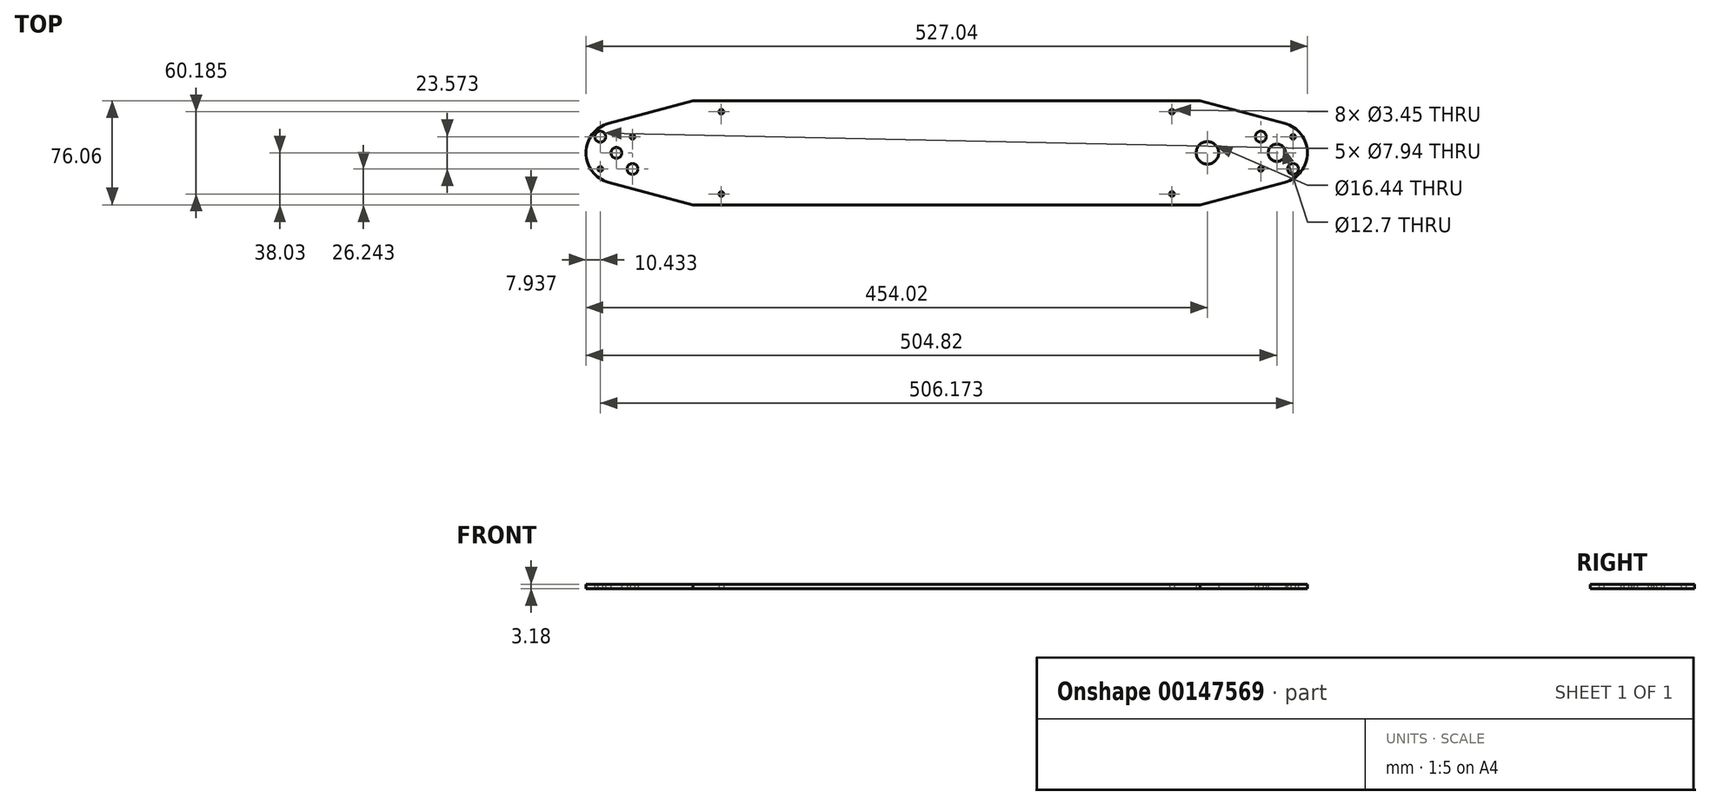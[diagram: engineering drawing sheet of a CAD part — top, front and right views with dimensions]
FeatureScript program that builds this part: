
annotation { "Feature Type Name" : "Feature", "Feature Type Description" : "" }
export const myFeature = defineFeature(function(context is Context, id is Id, definition is map)
    precondition{}
    {
        {
            var Q0;
            Q0=qCreatedBy(makeId("Top.planeOp"),FACE);
            var sketch = newSketch(context, id + "F0", { "sketchPlane" : qUnion([Q0])});
            skPoint(sketch, "E0.rect.middle", {"position": v(0, 0) * mm});
            skCircle(sketch, "E1", {"center": v(0, 0) * mm, "radius": 11.11 * mm, "construction": true});
            skLineSegment(sketch, "E2.bottom", {"start": v(11.79, 11.79) * mm, "end": v(-11.79, 11.79) * mm, "construction": true});
            skLineSegment(sketch, "E2.left", {"start": v(11.79, 11.79) * mm, "end": v(11.79, -11.79) * mm, "construction": true});
            skLineSegment(sketch, "E2.right", {"start": v(-11.79, 11.79) * mm, "end": v(-11.79, -11.79) * mm, "construction": true});
            skCircle(sketch, "E3", {"center": v(11.79, 11.79) * mm, "radius": 5.56 * mm, "construction": true});
            skCircle(sketch, "E4", {"center": v(-11.79, 11.79) * mm, "radius": 3.97 * mm});
            skCircle(sketch, "E5", {"center": v(11.79, 11.79) * mm, "radius": 1.73 * mm});
            skCircle(sketch, "E6", {"center": v(11.79, -11.79) * mm, "radius": 3.97 * mm});
            skCircle(sketch, "E7", {"center": v(-11.79, -11.79) * mm, "radius": 1.73 * mm});
            skArc(sketch, "E8", {"start": v(-488.35, 21.47) * mm, "mid": v(-504.83, 0) * mm, "end": v(-488.35, -21.47) * mm});
            skLineSegment(sketch, "E9.bottom", {"start": v(-494.39, 11.79) * mm, "end": v(-470.81, 11.79) * mm, "construction": true});
            skLineSegment(sketch, "E9.top", {"start": v(-494.39, -11.79) * mm, "end": v(-470.81, -11.79) * mm, "construction": true});
            skLineSegment(sketch, "E9.left", {"start": v(-494.39, 11.79) * mm, "end": v(-494.39, -11.79) * mm, "construction": true});
            skLineSegment(sketch, "E9.right", {"start": v(-470.81, 11.79) * mm, "end": v(-470.81, -11.79) * mm, "construction": true});
            skCircle(sketch, "E10", {"center": v(-470.81, 11.79) * mm, "radius": 1.73 * mm});
            skCircle(sketch, "E11", {"center": v(-482.6, 0) * mm, "radius": 3.97 * mm});
            skCircle(sketch, "E12", {"center": v(-494.39, 11.79) * mm, "radius": 3.97 * mm});
            skCircle(sketch, "E13", {"center": v(-494.39, -11.79) * mm, "radius": 1.73 * mm});
            skCircle(sketch, "E14", {"center": v(-470.81, -11.79) * mm, "radius": 3.97 * mm});
            skLineSegment(sketch, "E15", {"start": v(0, 0) * mm, "end": v(-482.6, 0) * mm, "construction": true});
            skLineSegment(sketch, "E16", {"start": v(-488.35, -21.47) * mm, "end": v(-426.54, -38.03) * mm});
            skLineSegment(sketch, "E17", {"start": v(-488.35, 21.47) * mm, "end": v(-426.54, 38.03) * mm});
            skLineSegment(sketch, "E18", {"start": v(-420.2, -34.86) * mm, "end": v(-62.4, -34.86) * mm, "construction": true});
            skLineSegment(sketch, "E19", {"start": v(-420.2, 34.86) * mm, "end": v(-62.4, 34.86) * mm, "construction": true});
            skLineSegment(sketch, "E20", {"start": v(-420.2, 38.03) * mm, "end": v(-420.2, 34.86) * mm, "construction": true});
            skLineSegment(sketch, "E21", {"start": v(-420.2, 38.03) * mm, "end": v(-426.54, 38.03) * mm});
            skLineSegment(sketch, "E22", {"start": v(-420.2, -34.86) * mm, "end": v(-420.2, -38.03) * mm, "construction": true});
            skLineSegment(sketch, "E23", {"start": v(-420.2, -38.03) * mm, "end": v(-426.54, -38.03) * mm});
            skLineSegment(sketch, "E24", {"start": v(-62.4, -34.86) * mm, "end": v(-62.4, -38.03) * mm, "construction": true});
            skLineSegment(sketch, "E25", {"start": v(-62.4, -38.03) * mm, "end": v(-56.06, -38.03) * mm});
            skLineSegment(sketch, "E26", {"start": v(-62.4, 34.86) * mm, "end": v(-62.4, 38.03) * mm, "construction": true});
            skLineSegment(sketch, "E27", {"start": v(-62.4, 38.03) * mm, "end": v(-56.06, 38.03) * mm});
            skLineSegment(sketch, "E28", {"start": v(-56.06, -38.03) * mm, "end": v(5.75, -21.47) * mm});
            skLineSegment(sketch, "E29", {"start": v(5.75, 21.47) * mm, "end": v(-56.06, 38.03) * mm});
            skArc(sketch, "E30", {"start": v(5.75, -21.47) * mm, "mid": v(22.23, 0) * mm, "end": v(5.75, 21.47) * mm});
            skLineSegment(sketch, "E31", {"start": v(-420.2, 34.86) * mm, "end": v(-420.2, 30.1) * mm, "construction": true});
            skLineSegment(sketch, "E32", {"start": v(-420.2, 30.1) * mm, "end": v(-405.9, 30.1) * mm, "construction": true});
            skLineSegment(sketch, "E33", {"start": v(-420.2, -34.86) * mm, "end": v(-420.2, -30.1) * mm, "construction": true});
            skLineSegment(sketch, "E34", {"start": v(-420.2, -30.1) * mm, "end": v(-405.9, -30.1) * mm, "construction": true});
            skLineSegment(sketch, "E35", {"start": v(-62.4, -34.86) * mm, "end": v(-62.4, -30.1) * mm, "construction": true});
            skLineSegment(sketch, "E36", {"start": v(-62.4, -30.1) * mm, "end": v(-76.7, -30.1) * mm, "construction": true});
            skLineSegment(sketch, "E37", {"start": v(-62.4, 34.86) * mm, "end": v(-62.4, 30.1) * mm, "construction": true});
            skLineSegment(sketch, "E38", {"start": v(-62.4, 30.1) * mm, "end": v(-76.7, 30.1) * mm, "construction": true});
            skCircle(sketch, "E39", {"center": v(-405.9, 30.1) * mm, "radius": 1.73 * mm});
            skCircle(sketch, "E40", {"center": v(-76.7, 30.1) * mm, "radius": 1.73 * mm});
            skCircle(sketch, "E41", {"center": v(-76.7, -30.1) * mm, "radius": 1.73 * mm});
            skCircle(sketch, "E42", {"center": v(-405.9, -30.1) * mm, "radius": 1.73 * mm});
            skLineSegment(sketch, "E43", {"start": v(-11.79, -11.79) * mm, "end": v(11.79, -11.79) * mm, "construction": true});
            skLineSegment(sketch, "E44", {"start": v(-241.3, -34.86) * mm, "end": v(-241.3, 0) * mm, "construction": true});
            skLineSegment(sketch, "E45", {"start": v(-241.3, 0) * mm, "end": v(-241.3, 34.86) * mm, "construction": true});
            skCircle(sketch, "E46", {"center": v(-50.8, 0) * mm, "radius": 8.22 * mm});
            skCircle(sketch, "E47", {"center": v(0, 0) * mm, "radius": 6.35 * mm});
            skCircle(sketch, "E48", {"center": v(-494.39, 11.79) * mm, "radius": 5.56 * mm, "construction": true});
            skLineSegment(sketch, "E49", {"start": v(-488.35, 21.47) * mm, "end": v(-457.45, 21.47) * mm, "construction": true});
            skLineSegment(sketch, "E50", {"start": v(-457.45, 21.47) * mm, "end": v(-457.45, 29.75) * mm, "construction": true});
            skLineSegment(sketch, "E51", {"start": v(-420.2, 38.03) * mm, "end": v(-62.4, 38.03) * mm});
            skLineSegment(sketch, "E52", {"start": v(-62.4, -38.03) * mm, "end": v(-420.2, -38.03) * mm});
            skSolve(sketch);
        }
        {
            var Q0;
            Q0=qSketchRegion(id+"F0",true);
            extrude(context, id + "F1", {"entities" : qUnion([Q0]), "depth" : 3.17 * mm});
        }
    });
